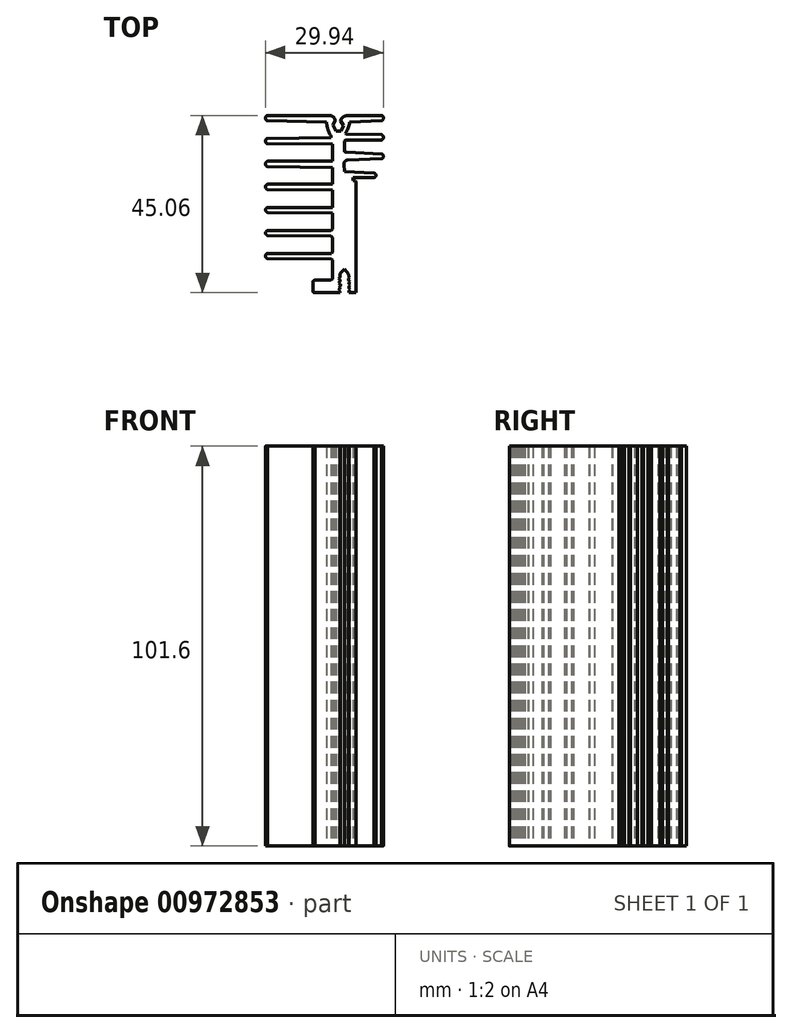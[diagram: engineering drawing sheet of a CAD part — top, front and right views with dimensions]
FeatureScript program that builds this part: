
annotation { "Feature Type Name" : "Feature", "Feature Type Description" : "" }
export const myFeature = defineFeature(function(context is Context, id is Id, definition is map)
    precondition{}
    {
        {
            var Q0;
            Q0=qCreatedBy(makeId("Top.planeOp"),FACE);
            var sketch = newSketch(context, id + "F0", { "sketchPlane" : qUnion([Q0])});
            skArc(sketch, "E0", {"start": v(-19.63, 24.8) * mm, "mid": v(-20, 24.2) * mm, "end": v(-19.66, 23.58) * mm});
            skArc(sketch, "E1", {"start": v(-19.66, 18.97) * mm, "mid": v(-20, 18.35) * mm, "end": v(-19.66, 17.74) * mm});
            skArc(sketch, "E2", {"start": v(-19.5, 13.21) * mm, "mid": v(-20.02, 12.52) * mm, "end": v(-19.5, 11.83) * mm});
            skArc(sketch, "E3", {"start": v(-19.5, 7.36) * mm, "mid": v(-20.02, 6.7) * mm, "end": v(-19.5, 6.04) * mm});
            skArc(sketch, "E4", {"start": v(-19.5, 1.5) * mm, "mid": v(-20, 0.85) * mm, "end": v(-19.5, 0.21) * mm});
            skArc(sketch, "E5", {"start": v(-19.5, -4.38) * mm, "mid": v(-20, -5.02) * mm, "end": v(-19.5, -5.66) * mm});
            skArc(sketch, "E6", {"start": v(-19.5, -10.19) * mm, "mid": v(-20.02, -10.85) * mm, "end": v(-19.5, -11.52) * mm});
            skArc(sketch, "E7", {"start": v(-7.43, -17.03) * mm, "mid": v(-7.79, -17.13) * mm, "end": v(-7.96, -17.46) * mm});
            skArc(sketch, "E8", {"start": v(-7.96, -19.74) * mm, "mid": v(-7.84, -20.08) * mm, "end": v(-7.5, -20.18) * mm});
            skArc(sketch, "E9", {"start": v(7.58, 9.06) * mm, "mid": v(8.03, 9.65) * mm, "end": v(7.56, 10.22) * mm});
            skArc(sketch, "E10", {"start": v(9.51, 13.84) * mm, "mid": v(9.9, 14.43) * mm, "end": v(9.57, 15.06) * mm});
            skArc(sketch, "E11", {"start": v(9.57, 18.65) * mm, "mid": v(9.92, 19.3) * mm, "end": v(9.57, 19.94) * mm});
            skArc(sketch, "E12", {"start": v(9.57, 23.53) * mm, "mid": v(9.92, 24.2) * mm, "end": v(9.57, 24.87) * mm});
            skArc(sketch, "E13", {"start": v(-2.35, 23.55) * mm, "mid": v(-2.65, 24.34) * mm, "end": v(-3.37, 24.8) * mm});
            skArc(sketch, "E14", {"start": v(0.52, 24.8) * mm, "mid": v(-0.4, 24.39) * mm, "end": v(-0.96, 23.55) * mm});
            skArc(sketch, "E15", {"start": v(0.32, 20.28) * mm, "mid": v(1, 21.67) * mm, "end": v(1.37, 23.18) * mm});
            skArc(sketch, "E16", {"start": v(-4.5, 23.18) * mm, "mid": v(-4.16, 21.33) * mm, "end": v(-3.38, 19.62) * mm});
            skArc(sketch, "E17", {"start": v(0.63, 18.65) * mm, "mid": v(0.22, 18.5) * mm, "end": v(0, 18.12) * mm});
            skArc(sketch, "E18", {"start": v(0, 15.94) * mm, "mid": v(0.21, 15.6) * mm, "end": v(0.6, 15.51) * mm});
            skArc(sketch, "E19", {"start": v(0.87, 13.54) * mm, "mid": v(0.13, 13.13) * mm, "end": v(-0.1, 12.31) * mm});
            skLineSegment(sketch, "E20", {"start": v(0.52, 24.8) * mm, "end": v(9.57, 24.87) * mm});
            skLineSegment(sketch, "E21", {"start": v(9.57, 23.53) * mm, "end": v(1.37, 23.18) * mm});
            skLineSegment(sketch, "E22", {"start": v(0.32, 20.28) * mm, "end": v(0.37, 20.08) * mm});
            skLineSegment(sketch, "E23", {"start": v(0.37, 20.08) * mm, "end": v(9.57, 19.94) * mm});
            skLineSegment(sketch, "E24", {"start": v(0.63, 18.65) * mm, "end": v(9.57, 18.65) * mm});
            skLineSegment(sketch, "E25", {"start": v(0, 18.12) * mm, "end": v(0, 15.94) * mm});
            skLineSegment(sketch, "E26", {"start": v(0.6, 15.51) * mm, "end": v(9.57, 15.06) * mm});
            skLineSegment(sketch, "E27", {"start": v(9.51, 13.84) * mm, "end": v(0.87, 13.54) * mm});
            skLineSegment(sketch, "E28", {"start": v(-0.1, 12.31) * mm, "end": v(0, 11.13) * mm});
            skLineSegment(sketch, "E29", {"start": v(0, 11.13) * mm, "end": v(0.04, 10.63) * mm});
            skLineSegment(sketch, "E30", {"start": v(0.04, 10.63) * mm, "end": v(7.56, 10.22) * mm});
            skLineSegment(sketch, "E31", {"start": v(7.58, 9.06) * mm, "end": v(2.15, 9.06) * mm});
            skLineSegment(sketch, "E32", {"start": v(2.15, 9.06) * mm, "end": v(2.15, 8.25) * mm});
            skLineSegment(sketch, "E33", {"start": v(2.15, 8.25) * mm, "end": v(2.83, 8.25) * mm});
            skLineSegment(sketch, "E34", {"start": v(2.83, 8.25) * mm, "end": v(2.97, 7.73) * mm});
            skLineSegment(sketch, "E35", {"start": v(2.97, 7.73) * mm, "end": v(2.97, -20.18) * mm});
            skLineSegment(sketch, "E36", {"start": v(2.97, -20.18) * mm, "end": v(1.15, -20.18) * mm});
            skLineSegment(sketch, "E37", {"start": v(1.15, -20.18) * mm, "end": v(1.15, -19.6) * mm});
            skLineSegment(sketch, "E38", {"start": v(1.15, -19.6) * mm, "end": v(1.5, -19.36) * mm});
            skLineSegment(sketch, "E39", {"start": v(1.5, -19.36) * mm, "end": v(1.13, -19.15) * mm});
            skLineSegment(sketch, "E40", {"start": v(1.13, -19.15) * mm, "end": v(1.13, -18.5) * mm});
            skLineSegment(sketch, "E41", {"start": v(1.13, -18.5) * mm, "end": v(1.44, -18.27) * mm});
            skLineSegment(sketch, "E42", {"start": v(1.44, -18.27) * mm, "end": v(1.13, -18.03) * mm});
            skLineSegment(sketch, "E43", {"start": v(1.13, -18.03) * mm, "end": v(1.14, -17.57) * mm});
            skLineSegment(sketch, "E44", {"start": v(1.14, -17.57) * mm, "end": v(1.46, -17.34) * mm});
            skLineSegment(sketch, "E45", {"start": v(1.46, -17.34) * mm, "end": v(1.05, -17.06) * mm});
            skLineSegment(sketch, "E46", {"start": v(1.05, -17.06) * mm, "end": v(1.02, -16.56) * mm});
            skLineSegment(sketch, "E47", {"start": v(1.02, -16.56) * mm, "end": v(1.37, -16.31) * mm});
            skLineSegment(sketch, "E48", {"start": v(1.37, -16.31) * mm, "end": v(1.13, -16.16) * mm});
            skLineSegment(sketch, "E49", {"start": v(1.13, -16.16) * mm, "end": v(1.1, -15.42) * mm});
            skLineSegment(sketch, "E50", {"start": v(1.1, -15.42) * mm, "end": v(0, -14.2) * mm});
            skLineSegment(sketch, "E51", {"start": v(0, -14.2) * mm, "end": v(-1.14, -15.32) * mm});
            skLineSegment(sketch, "E52", {"start": v(-1.14, -15.32) * mm, "end": v(-1.14, -16.39) * mm});
            skLineSegment(sketch, "E53", {"start": v(-1.14, -16.39) * mm, "end": v(-1.42, -16.59) * mm});
            skLineSegment(sketch, "E54", {"start": v(-1.42, -16.59) * mm, "end": v(-1.14, -16.89) * mm});
            skLineSegment(sketch, "E55", {"start": v(-1.14, -16.89) * mm, "end": v(-1.14, -17.35) * mm});
            skLineSegment(sketch, "E56", {"start": v(-1.14, -17.35) * mm, "end": v(-1.44, -17.71) * mm});
            skLineSegment(sketch, "E57", {"start": v(-1.44, -17.71) * mm, "end": v(-1.02, -17.94) * mm});
            skLineSegment(sketch, "E58", {"start": v(-1.02, -17.94) * mm, "end": v(-1.02, -18.5) * mm});
            skLineSegment(sketch, "E59", {"start": v(-1.02, -18.5) * mm, "end": v(-1.3, -18.7) * mm});
            skLineSegment(sketch, "E60", {"start": v(-1.3, -18.7) * mm, "end": v(-1.14, -18.93) * mm});
            skLineSegment(sketch, "E61", {"start": v(-1.14, -18.93) * mm, "end": v(-1.16, -19.3) * mm});
            skLineSegment(sketch, "E62", {"start": v(-1.16, -19.3) * mm, "end": v(-1.42, -19.57) * mm});
            skLineSegment(sketch, "E63", {"start": v(-1.42, -19.57) * mm, "end": v(-1.14, -19.84) * mm});
            skLineSegment(sketch, "E64", {"start": v(-1.14, -19.84) * mm, "end": v(-1.16, -20.17) * mm});
            skLineSegment(sketch, "E65", {"start": v(-1.16, -20.17) * mm, "end": v(-7.5, -20.18) * mm});
            skLineSegment(sketch, "E66", {"start": v(-7.96, -19.74) * mm, "end": v(-7.96, -17.46) * mm});
            skLineSegment(sketch, "E67", {"start": v(-7.43, -17.03) * mm, "end": v(-3.37, -17.03) * mm});
            skLineSegment(sketch, "E68", {"start": v(-3.37, -17.03) * mm, "end": v(-3.02, -16.77) * mm});
            skLineSegment(sketch, "E69", {"start": v(-3.02, -16.77) * mm, "end": v(-3.02, -11.94) * mm});
            skLineSegment(sketch, "E70", {"start": v(-3.02, -11.94) * mm, "end": v(-3.25, -11.61) * mm});
            skLineSegment(sketch, "E71", {"start": v(-3.25, -11.61) * mm, "end": v(-19.5, -11.52) * mm});
            skLineSegment(sketch, "E72", {"start": v(-19.5, -10.19) * mm, "end": v(-3.25, -10.19) * mm});
            skLineSegment(sketch, "E73", {"start": v(-3.25, -10.19) * mm, "end": v(-3.02, -9.78) * mm});
            skLineSegment(sketch, "E74", {"start": v(-3.02, -9.78) * mm, "end": v(-3.02, -6.13) * mm});
            skLineSegment(sketch, "E75", {"start": v(-3.02, -6.13) * mm, "end": v(-3.37, -5.77) * mm});
            skLineSegment(sketch, "E76", {"start": v(-3.37, -5.77) * mm, "end": v(-19.5, -5.66) * mm});
            skLineSegment(sketch, "E77", {"start": v(-19.5, -4.38) * mm, "end": v(-3.37, -4.38) * mm});
            skLineSegment(sketch, "E78", {"start": v(-3.37, -4.38) * mm, "end": v(-3.02, -3.95) * mm});
            skLineSegment(sketch, "E79", {"start": v(-3.02, -3.95) * mm, "end": v(-3.02, 0) * mm});
            skLineSegment(sketch, "E80", {"start": v(-3.02, 0) * mm, "end": v(-19.5, 0.21) * mm});
            skLineSegment(sketch, "E81", {"start": v(-3.02, 1.5) * mm, "end": v(-2.96, 5.85) * mm});
            skLineSegment(sketch, "E82", {"start": v(-2.96, 5.85) * mm, "end": v(-19.5, 6.04) * mm});
            skLineSegment(sketch, "E83", {"start": v(-19.5, 7.36) * mm, "end": v(-3.02, 7.36) * mm});
            skLineSegment(sketch, "E84", {"start": v(-3.02, 7.36) * mm, "end": v(-3.02, 11.63) * mm});
            skLineSegment(sketch, "E85", {"start": v(-3.02, 11.63) * mm, "end": v(-19.5, 11.83) * mm});
            skLineSegment(sketch, "E86", {"start": v(-19.5, 1.5) * mm, "end": v(-3.02, 1.5) * mm});
            skLineSegment(sketch, "E87", {"start": v(-19.5, 13.21) * mm, "end": v(-3.02, 13.21) * mm});
            skLineSegment(sketch, "E88", {"start": v(-3.02, 13.21) * mm, "end": v(-2.96, 17.6) * mm});
            skLineSegment(sketch, "E89", {"start": v(-2.96, 17.6) * mm, "end": v(-19.66, 17.74) * mm});
            skLineSegment(sketch, "E90", {"start": v(-19.66, 18.97) * mm, "end": v(-3.39, 19.2) * mm});
            skLineSegment(sketch, "E91", {"start": v(-3.39, 19.2) * mm, "end": v(-3.38, 19.62) * mm});
            skLineSegment(sketch, "E92", {"start": v(-4.5, 23.18) * mm, "end": v(-19.66, 23.58) * mm});
            skLineSegment(sketch, "E93", {"start": v(-19.63, 24.8) * mm, "end": v(-3.37, 24.8) * mm});
            skLineSegment(sketch, "E94", {"start": v(-2.35, 23.55) * mm, "end": v(-2.9, 22.39) * mm});
            skLineSegment(sketch, "E95", {"start": v(-2.9, 22.39) * mm, "end": v(-2.15, 20.86) * mm});
            skLineSegment(sketch, "E96", {"start": v(-2.15, 20.86) * mm, "end": v(-0.87, 20.84) * mm});
            skLineSegment(sketch, "E97", {"start": v(-0.87, 20.84) * mm, "end": v(-0.18, 22.29) * mm});
            skLineSegment(sketch, "E98", {"start": v(-0.18, 22.29) * mm, "end": v(-0.96, 23.55) * mm});
            skSolve(sketch);
        }
        {
            var Q0;
            Q0=makeQuery(id+"F0.imprint","IMPRINT",FACE,{"disambiguationData":[TD([[makeQuery(id+"F0.imprint","IMPRINT",EDGE,{"derivedFrom":sQuery(id+"F0.wireOp",EDGE,"E0")}),1.0]])]});
            extrude(context, id + "F1", {"entities" : qUnion([Q0]), "depth" : 50.8 * mm, "offsetDistance" : 25.4 * mm, "hasSecondDirection" : true, "secondDirectionOppositeDirection" : true, "secondDirectionDepth" : 50.8 * mm});
        }
        {
            var Q0;
            Q0=qCreatedBy(makeId("Top.planeOp"),FACE);
            var sketch = newSketch(context, id + "F2", { "sketchPlane" : qUnion([Q0])});
            skLineSegment(sketch, "E99", {"start": v(0, -36.38) * mm, "end": v(0, -49.93) * mm, "construction": true});
            skLineSegment(sketch, "E100", {"start": v(0, -49.93) * mm, "end": v(-1.05, -49.93) * mm});
            skLineSegment(sketch, "E101", {"start": v(-1.05, -49.93) * mm, "end": v(-1.05, -48.93) * mm});
            skLineSegment(sketch, "E102", {"start": v(-1.05, -48.93) * mm, "end": v(-0.8, -48.93) * mm});
            skLineSegment(sketch, "E103", {"start": v(-0.8, -48.93) * mm, "end": v(-0.8, -48.68) * mm});
            skLineSegment(sketch, "E104", {"start": v(-0.8, -48.68) * mm, "end": v(-1.05, -48.68) * mm});
            skLineSegment(sketch, "E105", {"start": v(-1.05, -48.68) * mm, "end": v(-1.05, -46.93) * mm});
            skLineSegment(sketch, "E106", {"start": v(-1.05, -46.93) * mm, "end": v(-2.05, -46.93) * mm});
            skLineSegment(sketch, "E107", {"start": v(-2.05, -46.93) * mm, "end": v(-2.05, -43.93) * mm});
            skLineSegment(sketch, "E108", {"start": v(-2.05, -43.93) * mm, "end": v(-1.55, -43.93) * mm});
            skLineSegment(sketch, "E109", {"start": v(-1.55, -43.93) * mm, "end": v(-1.55, -39.43) * mm});
            skLineSegment(sketch, "E110", {"start": v(-1.55, -39.43) * mm, "end": v(0, -39.43) * mm});
            skSolve(sketch);
        }
        {
            var Q0;
            Q0=sQuery(id+"F2.wireOp",EDGE,"E110");
            var Q1;
            Q1=sQuery(id+"F2.wireOp",EDGE,"E109");
            var Q2;
            Q2=sQuery(id+"F2.wireOp",EDGE,"E107");
            var Q3;
            Q3=sQuery(id+"F2.wireOp",EDGE,"E108");
            var Q4;
            Q4=sQuery(id+"F2.wireOp",EDGE,"E106");
            var Q5;
            Q5=sQuery(id+"F2.wireOp",EDGE,"E105");
            var Q6;
            Q6=sQuery(id+"F2.wireOp",EDGE,"E104");
            var Q7;
            Q7=sQuery(id+"F2.wireOp",EDGE,"E103");
            var Q8;
            Q8=sQuery(id+"F2.wireOp",EDGE,"E102");
            var Q9;
            Q9=sQuery(id+"F2.wireOp",EDGE,"E101");
            var Q10;
            Q10=sQuery(id+"F2.wireOp",EDGE,"E100");
            var Q11;
            Q11=sQuery(id+"F2.wireOp",EDGE,"E99");
            revolve(context, id + "F3", {"bodyType" : ToolBodyType.SURFACE, "surfaceOperationType" : NewSurfaceOperationType.NEW, "surfaceEntities" : qUnion([Q0, Q1, Q2, Q3, Q4, Q5, Q6, Q7, Q8, Q9, Q10]), "axis" : qUnion([Q11]), "revolveType" : RevolveType.FULL});
        }
        {
            var Q0;
            Q0=makeQuery(id+"F3.opRevolve","SWEPT_EDGE",EDGE,{"disambiguationData":[OSD([sQuery(id+"F2.wireOp",VERTEX,"E109.end")])]});
            chamfer(context, id + "F4", {"entities" : qUnion([Q0]), "width" : 0.5 * mm, "tangentPropagation" : true});
        }
    });
